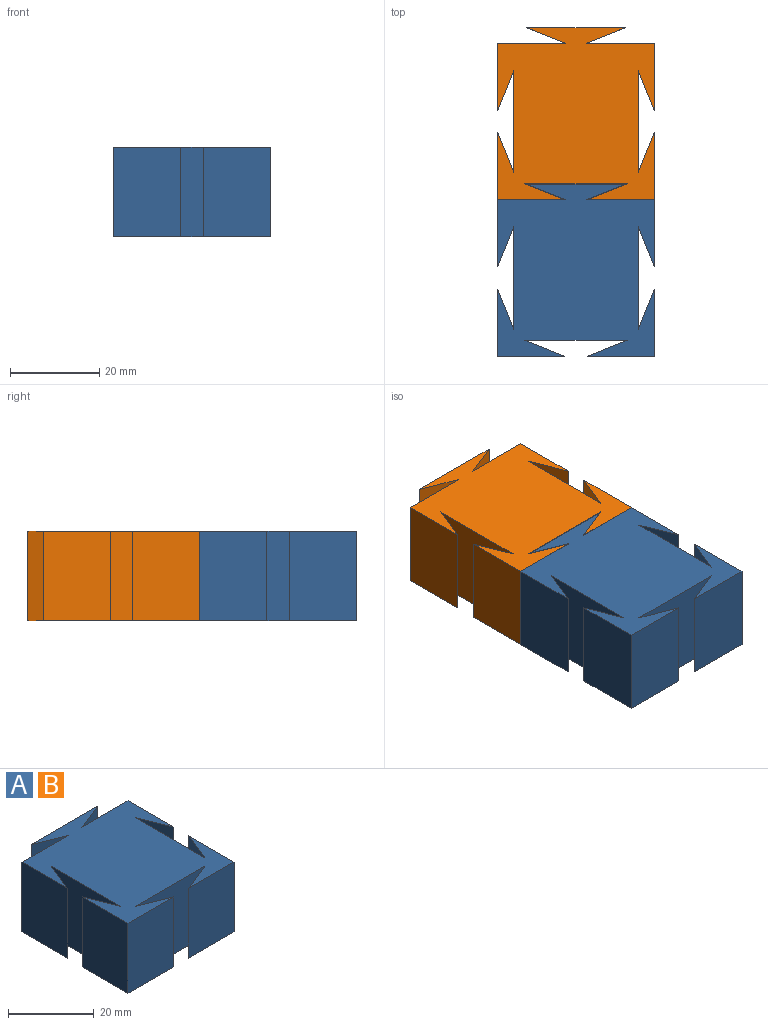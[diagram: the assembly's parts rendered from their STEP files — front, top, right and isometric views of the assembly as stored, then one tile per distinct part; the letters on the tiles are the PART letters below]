
ASSEMBLY  parts=2 mates=1
PART A: 22 faces, bbox 35x38.5x20 mm
  f0: plane 20x15.25mm, normal (0,1,0), area 305mm2, adj f1,f19,f20,f21
  f1: plane 20x15mm, normal (-1,0,0), area 300mm2, adj f0,f2,f20,f21
  f2: plane 20x9mm, normal (0.93,-0.37,0), area 193.9mm2, adj f1,f3,f20,f21
  f3: plane 23x20mm, normal (-1,0,0), area 460mm2, adj f2,f4,f20,f21
  f4: plane 20x9mm, normal (0.93,0.37,0), area 193.9mm2, adj f3,f5,f20,f21
  f5: plane 20x15mm, normal (-1,0,0), area 300mm2, adj f4,f6,f20,f21
  f6: plane 20x15mm, normal (0,-1,0), area 300mm2, adj f5,f7,f20,f21
  f7: plane 20x9mm, normal (0.37,0.93,0), area 193.9mm2, adj f6,f8,f20,f21
  f8: plane 23x20mm, normal (0,-1,0), area 460mm2, adj f7,f9,f20,f21
  f9: plane 20x9mm, normal (-0.37,0.93,0), area 193.9mm2, adj f8,f10,f20,f21
  f10: plane 20x15mm, normal (0,-1,0), area 300mm2, adj f9,f11,f20,f21
  f11: plane 20x15mm, normal (1,0,0), area 300mm2, adj f10,f12,f20,f21
  f12: plane 20x9mm, normal (-0.93,0.37,0), area 193.9mm2, adj f11,f13,f20,f21
  f13: plane 23x20mm, normal (1,0,0), area 460mm2, adj f12,f14,f20,f21
  f14: plane 20x9mm, normal (-0.93,-0.37,0), area 193.9mm2, adj f13,f15,f20,f21
  f15: plane 20x15mm, normal (1,0,0), area 300mm2, adj f14,f16,f20,f21
  f16: plane 20x15.25mm, normal (0,1,0), area 305mm2, adj f15,f17,f20,f21
  f17: plane 20x8.75mm, normal (0.37,-0.93,0), area 188.5mm2, adj f16,f18,f20,f21
  f18: plane 22x20mm, normal (0,1,0), area 440mm2, adj f17,f19,f20,f21
  f19: plane 20x8.75mm, normal (-0.37,-0.93,0), area 188.5mm2, adj f0,f18,f20,f21
  f20: plane 38.5x35mm, normal (0,0,1), area 1119.9mm2, adj f0,f1,f2,f3,f4,f5,f6,f7
  f21: plane 38.5x35mm, normal (0,0,-1), area 1119.9mm2, adj f0,f1,f2,f3,f4,f5,f6,f7
PART B: same geometry as A
PLACE A t=(3.7,-6.73,35.71)mm
PLACE B t=(3.7,28.27,35.71)mm
MATE fastened A.f20 <-> B.f20  axis (0,0,1) through (21.2,10.77,55.71)mm
